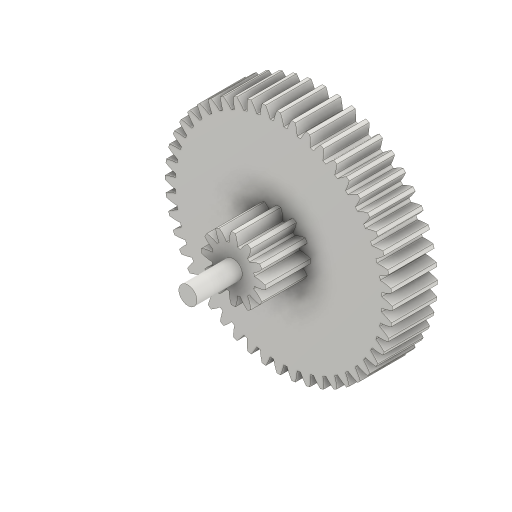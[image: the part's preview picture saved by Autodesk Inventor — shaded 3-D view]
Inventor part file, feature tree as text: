
AUTODESK INVENTOR PART (.ipt)
format: ipt  version: 2024 (Build 280153000, 153)  size: 445,440 bytes
history: native  units: mm (DEFAULTED — no unit token found)
features: extrude x3, plane x3, other x3, sketch x3
ambient origin geometry x8: Origin, YZ Plane, XZ Plane, XY Plane, X Axis, Y Axis, Z Axis, Center Point
bodies: Solid1 (feature_tree)
feature tree (12):
  extrude  "Extrusion1"  Depth=20.0mm TaperAngle=0.0deg
  plane  "Work Plane2"
  plane  "Work Plane8"
  plane  "Work Plane9"
  other  "Spur Gear"
  extrude  "Extrusion2"  Depth=10.0mm TaperAngle=0.0deg
  extrude  "Extrusion3"  Depth=20.0mm TaperAngle=0.0deg
  sketch  "Sketch1"  dims[d0=100.0mm d1=20.0mm d2=0.0mm]
  other  "Srf1"
  sketch  "Sketch3"  dims[d3=96.0mm d4=10.0mm d5=0.0mm]
  sketch  "Sketch4"  dims[d16=60.0mm d17=0.0mm d34=0.654498mm d39=0.0mm d41=0.0mm d43=60.0mm d46=60.0mm d47=0.0mm d48=0.0mm d49=20.0mm d50=0.0mm d51=8.0mm d52=20.0mm d53=0.0mm]
  other  "Pitch Diameter"
